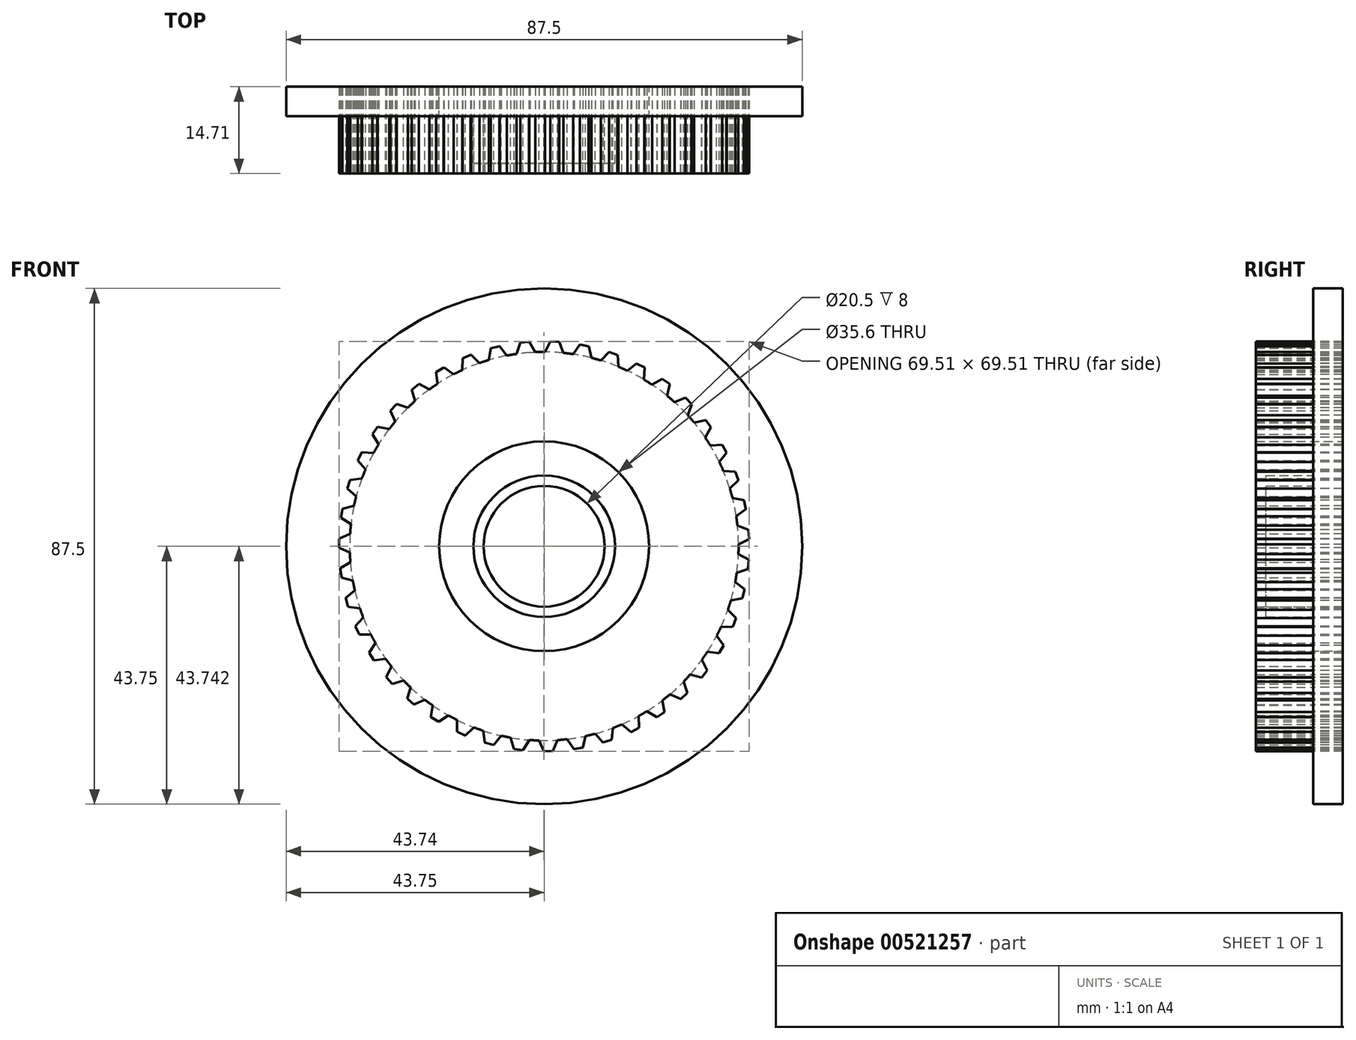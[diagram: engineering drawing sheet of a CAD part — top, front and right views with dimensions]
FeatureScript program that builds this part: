
annotation { "Feature Type Name" : "Feature", "Feature Type Description" : "" }
export const myFeature = defineFeature(function(context is Context, id is Id, definition is map)
    precondition{}
    {
        {
            var Q0;
            Q0=qCreatedBy(makeId("Front.planeOp"),FACE);
            var sketch = newSketch(context, id + "F0", { "sketchPlane" : qUnion([Q0])});
            skCircle(sketch, "E0", {"center": v(0, 0) * mm, "radius": 34.77 * mm, "construction": true});
            skCircle(sketch, "E1", {"center": v(0, 0) * mm, "radius": 10.25 * mm});
            skCircle(sketch, "E2", {"center": v(0, 0) * mm, "radius": 43.75 * mm});
            skCircle(sketch, "E3", {"center": v(0, 0) * mm, "radius": 12 * mm});
            skLineSegment(sketch, "E4", {"start": v(-2.5, 34.67) * mm, "end": v(2.5, 34.67) * mm, "construction": true});
            skCircle(sketch, "E5", {"center": v(0, 0) * mm, "radius": 32.97 * mm});
            skLineSegment(sketch, "E6", {"start": v(0, 0) * mm, "end": v(0, 46.74) * mm, "construction": true});
            skLineSegment(sketch, "E7", {"start": v(-2.5, 34.67) * mm, "end": v(-1.53, 32.93) * mm});
            skLineSegment(sketch, "E8", {"start": v(-1.53, 32.93) * mm, "end": v(0.13, 32.96) * mm});
            skLineSegment(sketch, "E9", {"start": v(0.13, 32.96) * mm, "end": v(1.03, 34.75) * mm});
            skLineSegment(sketch, "E10", {"start": v(1.03, 34.75) * mm, "end": v(2.5, 34.67) * mm});
            skLineSegment(sketch, "E11", {"start": v(-2.5, 34.67) * mm, "end": v(0, 0) * mm, "construction": true});
            skLineSegment(sketch, "E12", {"start": v(1.03, 34.75) * mm, "end": v(0, 0) * mm, "construction": true});
            skLineSegment(sketch, "E13", {"start": v(-2.5, 34.67) * mm, "end": v(-2.37, 32.88) * mm, "construction": true});
            skLineSegment(sketch, "E14", {"start": v(-2.37, 32.88) * mm, "end": v(0.13, 32.96) * mm});
            skLineSegment(sketch, "E15.1.0", {"start": v(-7.52, 33.94) * mm, "end": v(-6.3, 32.36) * mm});
            skLineSegment(sketch, "E15.1.1", {"start": v(-6.3, 32.36) * mm, "end": v(-4.67, 32.63) * mm});
            skLineSegment(sketch, "E15.1.2", {"start": v(-4.67, 32.63) * mm, "end": v(-4.05, 34.53) * mm});
            skLineSegment(sketch, "E15.1.3", {"start": v(-4.05, 34.53) * mm, "end": v(-2.58, 34.67) * mm});
            skLineSegment(sketch, "E15.2.0", {"start": v(-12.38, 32.48) * mm, "end": v(-10.95, 31.1) * mm});
            skLineSegment(sketch, "E15.2.1", {"start": v(-10.95, 31.1) * mm, "end": v(-9.37, 31.6) * mm});
            skLineSegment(sketch, "E15.2.2", {"start": v(-9.37, 31.6) * mm, "end": v(-9.03, 33.57) * mm});
            skLineSegment(sketch, "E15.2.3", {"start": v(-9.03, 33.57) * mm, "end": v(-7.6, 33.93) * mm});
            skLineSegment(sketch, "E15.3.0", {"start": v(-16.98, 30.34) * mm, "end": v(-15.36, 29.17) * mm});
            skLineSegment(sketch, "E15.3.1", {"start": v(-15.36, 29.17) * mm, "end": v(-13.88, 29.9) * mm});
            skLineSegment(sketch, "E15.3.2", {"start": v(-13.88, 29.9) * mm, "end": v(-13.82, 31.9) * mm});
            skLineSegment(sketch, "E15.3.3", {"start": v(-13.82, 31.9) * mm, "end": v(-12.45, 32.46) * mm});
            skLineSegment(sketch, "E15.4.0", {"start": v(-21.22, 27.54) * mm, "end": v(-19.44, 26.62) * mm});
            skLineSegment(sketch, "E15.4.1", {"start": v(-19.44, 26.62) * mm, "end": v(-18.08, 27.56) * mm});
            skLineSegment(sketch, "E15.4.2", {"start": v(-18.08, 27.56) * mm, "end": v(-18.32, 29.55) * mm});
            skLineSegment(sketch, "E15.4.3", {"start": v(-18.32, 29.55) * mm, "end": v(-17.05, 30.3) * mm});
            skLineSegment(sketch, "E15.5.0", {"start": v(-25, 24.16) * mm, "end": v(-23.11, 23.5) * mm});
            skLineSegment(sketch, "E15.5.1", {"start": v(-23.11, 23.5) * mm, "end": v(-21.9, 24.64) * mm});
            skLineSegment(sketch, "E15.5.2", {"start": v(-21.9, 24.64) * mm, "end": v(-22.43, 26.57) * mm});
            skLineSegment(sketch, "E15.5.3", {"start": v(-22.43, 26.57) * mm, "end": v(-21.28, 27.5) * mm});
            skLineSegment(sketch, "E15.6.0", {"start": v(-28.25, 20.26) * mm, "end": v(-26.29, 19.9) * mm});
            skLineSegment(sketch, "E15.6.1", {"start": v(-26.29, 19.9) * mm, "end": v(-25.26, 21.19) * mm});
            skLineSegment(sketch, "E15.6.2", {"start": v(-25.26, 21.19) * mm, "end": v(-26.05, 23.02) * mm});
            skLineSegment(sketch, "E15.6.3", {"start": v(-26.05, 23.02) * mm, "end": v(-25.05, 24.1) * mm});
            skLineSegment(sketch, "E15.7.0", {"start": v(-30.9, 15.93) * mm, "end": v(-28.9, 15.85) * mm});
            skLineSegment(sketch, "E15.7.1", {"start": v(-28.9, 15.85) * mm, "end": v(-28.07, 17.28) * mm});
            skLineSegment(sketch, "E15.7.2", {"start": v(-28.07, 17.28) * mm, "end": v(-29.13, 18.98) * mm});
            skLineSegment(sketch, "E15.7.3", {"start": v(-29.13, 18.98) * mm, "end": v(-28.3, 20.2) * mm});
            skLineSegment(sketch, "E15.8.0", {"start": v(-32.9, 11.26) * mm, "end": v(-30.9, 11.47) * mm});
            skLineSegment(sketch, "E15.8.1", {"start": v(-30.9, 11.47) * mm, "end": v(-30.29, 13.01) * mm});
            skLineSegment(sketch, "E15.8.2", {"start": v(-30.29, 13.01) * mm, "end": v(-31.58, 14.53) * mm});
            skLineSegment(sketch, "E15.8.3", {"start": v(-31.58, 14.53) * mm, "end": v(-30.94, 15.86) * mm});
            skLineSegment(sketch, "E15.9.0", {"start": v(-34.18, 6.35) * mm, "end": v(-32.25, 6.85) * mm});
            skLineSegment(sketch, "E15.9.1", {"start": v(-32.25, 6.85) * mm, "end": v(-31.86, 8.46) * mm});
            skLineSegment(sketch, "E15.9.2", {"start": v(-31.86, 8.46) * mm, "end": v(-33.36, 9.78) * mm});
            skLineSegment(sketch, "E15.9.3", {"start": v(-33.36, 9.78) * mm, "end": v(-32.92, 11.19) * mm});
            skLineSegment(sketch, "E15.10.0", {"start": v(-34.74, 1.3) * mm, "end": v(-32.9, 2.08) * mm});
            skLineSegment(sketch, "E15.10.1", {"start": v(-32.9, 2.08) * mm, "end": v(-32.75, 3.73) * mm});
            skLineSegment(sketch, "E15.10.2", {"start": v(-32.75, 3.73) * mm, "end": v(-34.43, 4.82) * mm});
            skLineSegment(sketch, "E15.10.3", {"start": v(-34.43, 4.82) * mm, "end": v(-34.2, 6.28) * mm});
            skLineSegment(sketch, "E15.11.0", {"start": v(-34.56, -3.76) * mm, "end": v(-32.85, -2.73) * mm});
            skLineSegment(sketch, "E15.11.1", {"start": v(-32.85, -2.73) * mm, "end": v(-32.95, -1.08) * mm});
            skLineSegment(sketch, "E15.11.2", {"start": v(-32.95, -1.08) * mm, "end": v(-34.76, -0.24) * mm});
            skLineSegment(sketch, "E15.11.3", {"start": v(-34.76, -0.24) * mm, "end": v(-34.74, 1.23) * mm});
            skLineSegment(sketch, "E15.12.0", {"start": v(-33.64, -8.76) * mm, "end": v(-32.1, -7.48) * mm});
            skLineSegment(sketch, "E15.12.1", {"start": v(-32.1, -7.48) * mm, "end": v(-32.44, -5.86) * mm});
            skLineSegment(sketch, "E15.12.2", {"start": v(-32.44, -5.86) * mm, "end": v(-34.36, -5.3) * mm});
            skLineSegment(sketch, "E15.12.3", {"start": v(-34.36, -5.3) * mm, "end": v(-34.55, -3.84) * mm});
            skLineSegment(sketch, "E15.13.0", {"start": v(-32.01, -13.56) * mm, "end": v(-30.67, -12.08) * mm});
            skLineSegment(sketch, "E15.13.1", {"start": v(-30.67, -12.08) * mm, "end": v(-31.24, -10.52) * mm});
            skLineSegment(sketch, "E15.13.2", {"start": v(-31.24, -10.52) * mm, "end": v(-33.22, -10.25) * mm});
            skLineSegment(sketch, "E15.13.3", {"start": v(-33.22, -10.25) * mm, "end": v(-33.62, -8.83) * mm});
            skLineSegment(sketch, "E15.14.0", {"start": v(-29.7, -18.08) * mm, "end": v(-28.59, -16.42) * mm});
            skLineSegment(sketch, "E15.14.1", {"start": v(-28.59, -16.42) * mm, "end": v(-29.38, -14.96) * mm});
            skLineSegment(sketch, "E15.14.2", {"start": v(-29.38, -14.96) * mm, "end": v(-31.37, -14.98) * mm});
            skLineSegment(sketch, "E15.14.3", {"start": v(-31.37, -14.98) * mm, "end": v(-31.98, -13.63) * mm});
            skLineSegment(sketch, "E15.15.0", {"start": v(-26.75, -22.2) * mm, "end": v(-25.9, -20.4) * mm});
            skLineSegment(sketch, "E15.15.1", {"start": v(-25.9, -20.4) * mm, "end": v(-26.88, -19.08) * mm});
            skLineSegment(sketch, "E15.15.2", {"start": v(-26.88, -19.08) * mm, "end": v(-28.86, -19.39) * mm});
            skLineSegment(sketch, "E15.15.3", {"start": v(-28.86, -19.39) * mm, "end": v(-29.66, -18.14) * mm});
            skLineSegment(sketch, "E15.16.0", {"start": v(-23.23, -25.87) * mm, "end": v(-22.65, -23.96) * mm});
            skLineSegment(sketch, "E15.16.1", {"start": v(-22.65, -23.96) * mm, "end": v(-23.82, -22.79) * mm});
            skLineSegment(sketch, "E15.16.2", {"start": v(-23.82, -22.79) * mm, "end": v(-25.73, -23.38) * mm});
            skLineSegment(sketch, "E15.16.3", {"start": v(-25.73, -23.38) * mm, "end": v(-26.7, -22.27) * mm});
            skLineSegment(sketch, "E15.17.0", {"start": v(-19.21, -28.97) * mm, "end": v(-18.92, -27) * mm});
            skLineSegment(sketch, "E15.17.1", {"start": v(-18.92, -27) * mm, "end": v(-20.25, -26.01) * mm});
            skLineSegment(sketch, "E15.17.2", {"start": v(-20.25, -26.01) * mm, "end": v(-22.05, -26.88) * mm});
            skLineSegment(sketch, "E15.17.3", {"start": v(-22.05, -26.88) * mm, "end": v(-23.17, -25.92) * mm});
            skLineSegment(sketch, "E15.18.0", {"start": v(-14.8, -31.46) * mm, "end": v(-14.78, -29.46) * mm});
            skLineSegment(sketch, "E15.18.1", {"start": v(-14.78, -29.46) * mm, "end": v(-16.25, -28.68) * mm});
            skLineSegment(sketch, "E15.18.2", {"start": v(-16.25, -28.68) * mm, "end": v(-17.9, -29.8) * mm});
            skLineSegment(sketch, "E15.18.3", {"start": v(-17.9, -29.8) * mm, "end": v(-19.15, -29.01) * mm});
            skLineSegment(sketch, "E15.19.0", {"start": v(-10.05, -33.28) * mm, "end": v(-10.34, -31.3) * mm});
            skLineSegment(sketch, "E15.19.1", {"start": v(-10.34, -31.3) * mm, "end": v(-11.9, -30.74) * mm});
            skLineSegment(sketch, "E15.19.2", {"start": v(-11.9, -30.74) * mm, "end": v(-13.37, -32.1) * mm});
            skLineSegment(sketch, "E15.19.3", {"start": v(-13.37, -32.1) * mm, "end": v(-14.72, -31.5) * mm});
            skLineSegment(sketch, "E15.20.0", {"start": v(-5.1, -34.39) * mm, "end": v(-5.67, -32.47) * mm});
            skLineSegment(sketch, "E15.20.1", {"start": v(-5.67, -32.47) * mm, "end": v(-7.3, -32.15) * mm});
            skLineSegment(sketch, "E15.20.2", {"start": v(-7.3, -32.15) * mm, "end": v(-8.56, -33.7) * mm});
            skLineSegment(sketch, "E15.20.3", {"start": v(-8.56, -33.7) * mm, "end": v(-9.98, -33.3) * mm});
            skLineSegment(sketch, "E15.21.0", {"start": v(-0.04, -34.76) * mm, "end": v(-0.88, -32.95) * mm});
            skLineSegment(sketch, "E15.21.1", {"start": v(-0.88, -32.95) * mm, "end": v(-2.53, -32.87) * mm});
            skLineSegment(sketch, "E15.21.2", {"start": v(-2.53, -32.87) * mm, "end": v(-3.56, -34.58) * mm});
            skLineSegment(sketch, "E15.21.3", {"start": v(-3.56, -34.58) * mm, "end": v(-5.02, -34.4) * mm});
            skLineSegment(sketch, "E15.22.0", {"start": v(5.02, -34.4) * mm, "end": v(3.93, -32.73) * mm});
            skLineSegment(sketch, "E15.22.1", {"start": v(3.93, -32.73) * mm, "end": v(2.28, -32.89) * mm});
            skLineSegment(sketch, "E15.22.2", {"start": v(2.28, -32.89) * mm, "end": v(1.51, -34.73) * mm});
            skLineSegment(sketch, "E15.22.3", {"start": v(1.51, -34.73) * mm, "end": v(0.04, -34.76) * mm});
            skLineSegment(sketch, "E15.23.0", {"start": v(9.98, -33.3) * mm, "end": v(8.65, -31.8) * mm});
            skLineSegment(sketch, "E15.23.1", {"start": v(8.65, -31.8) * mm, "end": v(7.04, -32.2) * mm});
            skLineSegment(sketch, "E15.23.2", {"start": v(7.04, -32.2) * mm, "end": v(6.55, -34.14) * mm});
            skLineSegment(sketch, "E15.23.3", {"start": v(6.55, -34.14) * mm, "end": v(5.1, -34.39) * mm});
            skLineSegment(sketch, "E15.24.0", {"start": v(14.72, -31.5) * mm, "end": v(13.2, -30.21) * mm});
            skLineSegment(sketch, "E15.24.1", {"start": v(13.2, -30.21) * mm, "end": v(11.66, -30.84) * mm});
            skLineSegment(sketch, "E15.24.2", {"start": v(11.66, -30.84) * mm, "end": v(11.46, -32.82) * mm});
            skLineSegment(sketch, "E15.24.3", {"start": v(11.46, -32.82) * mm, "end": v(10.05, -33.28) * mm});
            skLineSegment(sketch, "E15.25.0", {"start": v(19.15, -29.01) * mm, "end": v(17.45, -27.97) * mm});
            skLineSegment(sketch, "E15.25.1", {"start": v(17.45, -27.97) * mm, "end": v(16.02, -28.8) * mm});
            skLineSegment(sketch, "E15.25.2", {"start": v(16.02, -28.8) * mm, "end": v(16.11, -30.8) * mm});
            skLineSegment(sketch, "E15.25.3", {"start": v(16.11, -30.8) * mm, "end": v(14.8, -31.46) * mm});
            skLineSegment(sketch, "E15.26.0", {"start": v(23.17, -25.92) * mm, "end": v(21.33, -25.13) * mm});
            skLineSegment(sketch, "E15.26.1", {"start": v(21.33, -25.13) * mm, "end": v(20.05, -26.17) * mm});
            skLineSegment(sketch, "E15.26.2", {"start": v(20.05, -26.17) * mm, "end": v(20.43, -28.13) * mm});
            skLineSegment(sketch, "E15.26.3", {"start": v(20.43, -28.13) * mm, "end": v(19.21, -28.97) * mm});
            skLineSegment(sketch, "E15.27.0", {"start": v(26.7, -22.27) * mm, "end": v(24.77, -21.76) * mm});
            skLineSegment(sketch, "E15.27.1", {"start": v(24.77, -21.76) * mm, "end": v(23.64, -22.97) * mm});
            skLineSegment(sketch, "E15.27.2", {"start": v(23.64, -22.97) * mm, "end": v(24.3, -24.86) * mm});
            skLineSegment(sketch, "E15.27.3", {"start": v(24.3, -24.86) * mm, "end": v(23.23, -25.87) * mm});
            skLineSegment(sketch, "E15.28.0", {"start": v(29.66, -18.14) * mm, "end": v(27.67, -17.92) * mm});
            skLineSegment(sketch, "E15.28.1", {"start": v(27.67, -17.92) * mm, "end": v(26.74, -19.28) * mm});
            skLineSegment(sketch, "E15.28.2", {"start": v(26.74, -19.28) * mm, "end": v(27.67, -21.05) * mm});
            skLineSegment(sketch, "E15.28.3", {"start": v(27.67, -21.05) * mm, "end": v(26.75, -22.2) * mm});
            skLineSegment(sketch, "E15.29.0", {"start": v(31.98, -13.63) * mm, "end": v(29.98, -13.7) * mm});
            skLineSegment(sketch, "E15.29.1", {"start": v(29.98, -13.7) * mm, "end": v(29.26, -15.19) * mm});
            skLineSegment(sketch, "E15.29.2", {"start": v(29.26, -15.19) * mm, "end": v(30.44, -16.8) * mm});
            skLineSegment(sketch, "E15.29.3", {"start": v(30.44, -16.8) * mm, "end": v(29.7, -18.08) * mm});
            skLineSegment(sketch, "E15.30.0", {"start": v(33.62, -8.83) * mm, "end": v(31.66, -9.19) * mm});
            skLineSegment(sketch, "E15.30.1", {"start": v(31.66, -9.19) * mm, "end": v(31.16, -10.76) * mm});
            skLineSegment(sketch, "E15.30.2", {"start": v(31.16, -10.76) * mm, "end": v(32.56, -12.2) * mm});
            skLineSegment(sketch, "E15.30.3", {"start": v(32.56, -12.2) * mm, "end": v(32.01, -13.56) * mm});
            skLineSegment(sketch, "E15.31.0", {"start": v(34.55, -3.84) * mm, "end": v(32.66, -4.48) * mm});
            skLineSegment(sketch, "E15.31.1", {"start": v(32.66, -4.48) * mm, "end": v(32.4, -6.11) * mm});
            skLineSegment(sketch, "E15.31.2", {"start": v(32.4, -6.11) * mm, "end": v(33.99, -7.32) * mm});
            skLineSegment(sketch, "E15.31.3", {"start": v(33.99, -7.32) * mm, "end": v(33.64, -8.76) * mm});
            skLineSegment(sketch, "E15.32.0", {"start": v(34.74, 1.23) * mm, "end": v(32.96, 0.32) * mm});
            skLineSegment(sketch, "E15.32.1", {"start": v(32.96, 0.32) * mm, "end": v(32.94, -1.33) * mm});
            skLineSegment(sketch, "E15.32.2", {"start": v(32.94, -1.33) * mm, "end": v(34.69, -2.3) * mm});
            skLineSegment(sketch, "E15.32.3", {"start": v(34.69, -2.3) * mm, "end": v(34.56, -3.76) * mm});
            skLineSegment(sketch, "E15.33.0", {"start": v(34.2, 6.28) * mm, "end": v(32.56, 5.12) * mm});
            skLineSegment(sketch, "E15.33.1", {"start": v(32.56, 5.12) * mm, "end": v(32.78, 3.48) * mm});
            skLineSegment(sketch, "E15.33.2", {"start": v(32.78, 3.48) * mm, "end": v(34.65, 2.78) * mm});
            skLineSegment(sketch, "E15.33.3", {"start": v(34.65, 2.78) * mm, "end": v(34.74, 1.3) * mm});
            skLineSegment(sketch, "E15.34.0", {"start": v(32.92, 11.19) * mm, "end": v(31.47, 9.8) * mm});
            skLineSegment(sketch, "E15.34.1", {"start": v(31.47, 9.8) * mm, "end": v(31.93, 8.21) * mm});
            skLineSegment(sketch, "E15.34.2", {"start": v(31.93, 8.21) * mm, "end": v(33.88, 7.8) * mm});
            skLineSegment(sketch, "E15.34.3", {"start": v(33.88, 7.8) * mm, "end": v(34.18, 6.35) * mm});
            skLineSegment(sketch, "E15.35.0", {"start": v(30.94, 15.86) * mm, "end": v(29.7, 14.28) * mm});
            skLineSegment(sketch, "E15.35.1", {"start": v(29.7, 14.28) * mm, "end": v(30.39, 12.77) * mm});
            skLineSegment(sketch, "E15.35.2", {"start": v(30.39, 12.77) * mm, "end": v(32.38, 12.65) * mm});
            skLineSegment(sketch, "E15.35.3", {"start": v(32.38, 12.65) * mm, "end": v(32.9, 11.26) * mm});
            skLineSegment(sketch, "E15.36.0", {"start": v(28.3, 20.2) * mm, "end": v(27.31, 18.46) * mm});
            skLineSegment(sketch, "E15.36.1", {"start": v(27.31, 18.46) * mm, "end": v(28.2, 17.06) * mm});
            skLineSegment(sketch, "E15.36.2", {"start": v(28.2, 17.06) * mm, "end": v(30.2, 17.23) * mm});
            skLineSegment(sketch, "E15.36.3", {"start": v(30.2, 17.23) * mm, "end": v(30.9, 15.93) * mm});
            skLineSegment(sketch, "E15.37.0", {"start": v(25.05, 24.1) * mm, "end": v(24.33, 22.24) * mm});
            skLineSegment(sketch, "E15.37.1", {"start": v(24.33, 22.24) * mm, "end": v(25.42, 20.99) * mm});
            skLineSegment(sketch, "E15.37.2", {"start": v(25.42, 20.99) * mm, "end": v(27.37, 21.44) * mm});
            skLineSegment(sketch, "E15.37.3", {"start": v(27.37, 21.44) * mm, "end": v(28.25, 20.26) * mm});
            skLineSegment(sketch, "E15.38.0", {"start": v(21.28, 27.5) * mm, "end": v(20.84, 25.54) * mm});
            skLineSegment(sketch, "E15.38.1", {"start": v(20.84, 25.54) * mm, "end": v(22.1, 24.47) * mm});
            skLineSegment(sketch, "E15.38.2", {"start": v(22.1, 24.47) * mm, "end": v(23.95, 25.2) * mm});
            skLineSegment(sketch, "E15.38.3", {"start": v(23.95, 25.2) * mm, "end": v(25, 24.16) * mm});
            skLineSegment(sketch, "E15.39.0", {"start": v(17.05, 30.3) * mm, "end": v(16.9, 28.3) * mm});
            skLineSegment(sketch, "E15.39.1", {"start": v(16.9, 28.3) * mm, "end": v(18.3, 27.42) * mm});
            skLineSegment(sketch, "E15.39.2", {"start": v(18.3, 27.42) * mm, "end": v(20.03, 28.42) * mm});
            skLineSegment(sketch, "E15.39.3", {"start": v(20.03, 28.42) * mm, "end": v(21.22, 27.54) * mm});
            skLineSegment(sketch, "E15.40.0", {"start": v(12.45, 32.46) * mm, "end": v(12.6, 30.46) * mm});
            skLineSegment(sketch, "E15.40.1", {"start": v(12.6, 30.46) * mm, "end": v(14.1, 29.8) * mm});
            skLineSegment(sketch, "E15.40.2", {"start": v(14.1, 29.8) * mm, "end": v(15.68, 31.03) * mm});
            skLineSegment(sketch, "E15.40.3", {"start": v(15.68, 31.03) * mm, "end": v(16.98, 30.34) * mm});
            skLineSegment(sketch, "E15.41.0", {"start": v(7.6, 33.93) * mm, "end": v(8.02, 31.97) * mm});
            skLineSegment(sketch, "E15.41.1", {"start": v(8.02, 31.97) * mm, "end": v(9.62, 31.53) * mm});
            skLineSegment(sketch, "E15.41.2", {"start": v(9.62, 31.53) * mm, "end": v(11, 32.98) * mm});
            skLineSegment(sketch, "E15.41.3", {"start": v(11, 32.98) * mm, "end": v(12.38, 32.48) * mm});
            skLineSegment(sketch, "E15.42.0", {"start": v(2.58, 34.67) * mm, "end": v(3.28, 32.8) * mm});
            skLineSegment(sketch, "E15.42.1", {"start": v(3.28, 32.8) * mm, "end": v(4.93, 32.6) * mm});
            skLineSegment(sketch, "E15.42.2", {"start": v(4.93, 32.6) * mm, "end": v(6.07, 34.23) * mm});
            skLineSegment(sketch, "E15.42.3", {"start": v(6.07, 34.23) * mm, "end": v(7.52, 33.94) * mm});
            skLineSegment(sketch, "E16", {"start": v(2.5, 34.67) * mm, "end": v(2.58, 34.67) * mm});
            skLineSegment(sketch, "E17.1.0", {"start": v(-2.58, 34.67) * mm, "end": v(-2.5, 34.67) * mm});
            skLineSegment(sketch, "E17.2.0", {"start": v(-7.6, 33.93) * mm, "end": v(-7.52, 33.94) * mm});
            skLineSegment(sketch, "E17.3.0", {"start": v(-12.45, 32.46) * mm, "end": v(-12.38, 32.48) * mm});
            skLineSegment(sketch, "E17.4.0", {"start": v(-17.05, 30.3) * mm, "end": v(-16.98, 30.34) * mm});
            skLineSegment(sketch, "E17.5.0", {"start": v(-21.28, 27.5) * mm, "end": v(-21.22, 27.54) * mm});
            skLineSegment(sketch, "E17.6.0", {"start": v(-25.05, 24.1) * mm, "end": v(-25, 24.16) * mm});
            skLineSegment(sketch, "E17.7.0", {"start": v(-28.3, 20.2) * mm, "end": v(-28.25, 20.26) * mm});
            skLineSegment(sketch, "E17.8.0", {"start": v(-30.94, 15.86) * mm, "end": v(-30.9, 15.93) * mm});
            skLineSegment(sketch, "E17.9.0", {"start": v(-32.92, 11.19) * mm, "end": v(-32.9, 11.26) * mm});
            skLineSegment(sketch, "E17.10.0", {"start": v(-34.2, 6.28) * mm, "end": v(-34.18, 6.35) * mm});
            skLineSegment(sketch, "E17.11.0", {"start": v(-34.74, 1.23) * mm, "end": v(-34.74, 1.3) * mm});
            skLineSegment(sketch, "E17.12.0", {"start": v(-34.55, -3.84) * mm, "end": v(-34.56, -3.76) * mm});
            skLineSegment(sketch, "E17.13.0", {"start": v(-33.62, -8.83) * mm, "end": v(-33.64, -8.76) * mm});
            skLineSegment(sketch, "E17.14.0", {"start": v(-31.98, -13.63) * mm, "end": v(-32.01, -13.56) * mm});
            skLineSegment(sketch, "E17.15.0", {"start": v(-29.66, -18.14) * mm, "end": v(-29.7, -18.08) * mm});
            skLineSegment(sketch, "E17.16.0", {"start": v(-26.7, -22.27) * mm, "end": v(-26.75, -22.2) * mm});
            skLineSegment(sketch, "E17.17.0", {"start": v(-23.17, -25.92) * mm, "end": v(-23.23, -25.87) * mm});
            skLineSegment(sketch, "E17.18.0", {"start": v(-19.15, -29.01) * mm, "end": v(-19.21, -28.97) * mm});
            skLineSegment(sketch, "E17.19.0", {"start": v(-14.72, -31.5) * mm, "end": v(-14.8, -31.46) * mm});
            skLineSegment(sketch, "E17.20.0", {"start": v(-9.98, -33.3) * mm, "end": v(-10.05, -33.28) * mm});
            skLineSegment(sketch, "E17.21.0", {"start": v(-5.02, -34.4) * mm, "end": v(-5.1, -34.39) * mm});
            skLineSegment(sketch, "E17.22.0", {"start": v(0.04, -34.76) * mm, "end": v(-0.04, -34.76) * mm});
            skLineSegment(sketch, "E17.23.0", {"start": v(5.1, -34.39) * mm, "end": v(5.02, -34.4) * mm});
            skLineSegment(sketch, "E17.24.0", {"start": v(10.05, -33.28) * mm, "end": v(9.98, -33.3) * mm});
            skLineSegment(sketch, "E17.25.0", {"start": v(14.8, -31.46) * mm, "end": v(14.72, -31.5) * mm});
            skLineSegment(sketch, "E17.26.0", {"start": v(19.21, -28.97) * mm, "end": v(19.15, -29.01) * mm});
            skLineSegment(sketch, "E17.27.0", {"start": v(23.23, -25.87) * mm, "end": v(23.17, -25.92) * mm});
            skLineSegment(sketch, "E17.28.0", {"start": v(26.75, -22.2) * mm, "end": v(26.7, -22.27) * mm});
            skLineSegment(sketch, "E17.29.0", {"start": v(29.7, -18.08) * mm, "end": v(29.66, -18.14) * mm});
            skLineSegment(sketch, "E17.30.0", {"start": v(32.01, -13.56) * mm, "end": v(31.98, -13.63) * mm});
            skLineSegment(sketch, "E17.31.0", {"start": v(33.64, -8.76) * mm, "end": v(33.62, -8.83) * mm});
            skLineSegment(sketch, "E17.32.0", {"start": v(34.56, -3.76) * mm, "end": v(34.55, -3.84) * mm});
            skLineSegment(sketch, "E17.33.0", {"start": v(34.74, 1.3) * mm, "end": v(34.74, 1.23) * mm});
            skLineSegment(sketch, "E17.34.0", {"start": v(34.18, 6.35) * mm, "end": v(34.2, 6.28) * mm});
            skLineSegment(sketch, "E17.35.0", {"start": v(32.9, 11.26) * mm, "end": v(32.92, 11.19) * mm});
            skLineSegment(sketch, "E17.36.0", {"start": v(30.9, 15.93) * mm, "end": v(30.94, 15.86) * mm});
            skLineSegment(sketch, "E17.37.0", {"start": v(28.25, 20.26) * mm, "end": v(28.3, 20.2) * mm});
            skLineSegment(sketch, "E17.38.0", {"start": v(25, 24.16) * mm, "end": v(25.05, 24.1) * mm});
            skLineSegment(sketch, "E17.39.0", {"start": v(21.22, 27.54) * mm, "end": v(21.28, 27.5) * mm});
            skLineSegment(sketch, "E17.40.0", {"start": v(16.98, 30.34) * mm, "end": v(17.05, 30.3) * mm});
            skLineSegment(sketch, "E17.41.0", {"start": v(12.38, 32.48) * mm, "end": v(12.45, 32.46) * mm});
            skLineSegment(sketch, "E17.42.0", {"start": v(7.52, 33.94) * mm, "end": v(7.6, 33.93) * mm});
            skSolve(sketch);
        }
        {
            var Q0;
            {var subQ1=sQuery(id+"F0.wireOp",EDGE,"E15.4.0");Q0=makeQuery(id+"F0.imprint","IMPRINT",FACE,{"disambiguationData":[TD([[makeQuery(id+"F0.imprint","IMPRINT",EDGE,{"derivedFrom":subQ1}),-1.0]])]});}
            var Q1;
            {var subQ1=sQuery(id+"F0.wireOp",EDGE,"E15.28.0");Q1=makeQuery(id+"F0.imprint","IMPRINT",FACE,{"disambiguationData":[TD([[makeQuery(id+"F0.imprint","IMPRINT",EDGE,{"derivedFrom":subQ1}),-1.0]])]});}
            var Q2;
            {var subQ1=sQuery(id+"F0.wireOp",EDGE,"E15.41.0");Q2=makeQuery(id+"F0.imprint","IMPRINT",FACE,{"disambiguationData":[TD([[makeQuery(id+"F0.imprint","IMPRINT",EDGE,{"derivedFrom":subQ1}),-1.0]])]});}
            var Q3;
            {var subQ1=sQuery(id+"F0.wireOp",EDGE,"E15.2.0");Q3=makeQuery(id+"F0.imprint","IMPRINT",FACE,{"disambiguationData":[TD([[makeQuery(id+"F0.imprint","IMPRINT",EDGE,{"derivedFrom":subQ1}),-1.0]])]});}
            var Q4;
            {var subQ1=sQuery(id+"F0.wireOp",EDGE,"E15.10.0");Q4=makeQuery(id+"F0.imprint","IMPRINT",FACE,{"disambiguationData":[TD([[makeQuery(id+"F0.imprint","IMPRINT",EDGE,{"derivedFrom":subQ1}),-1.0]])]});}
            var Q5;
            {var subQ1=sQuery(id+"F0.wireOp",EDGE,"E15.26.0");Q5=makeQuery(id+"F0.imprint","IMPRINT",FACE,{"disambiguationData":[TD([[makeQuery(id+"F0.imprint","IMPRINT",EDGE,{"derivedFrom":subQ1}),-1.0]])]});}
            var Q6;
            {var subQ1=sQuery(id+"F0.wireOp",EDGE,"E15.18.0");Q6=makeQuery(id+"F0.imprint","IMPRINT",FACE,{"disambiguationData":[TD([[makeQuery(id+"F0.imprint","IMPRINT",EDGE,{"derivedFrom":subQ1}),-1.0]])]});}
            var Q7;
            {var subQ1=sQuery(id+"F0.wireOp",EDGE,"E15.6.0");Q7=makeQuery(id+"F0.imprint","IMPRINT",FACE,{"disambiguationData":[TD([[makeQuery(id+"F0.imprint","IMPRINT",EDGE,{"derivedFrom":subQ1}),-1.0]])]});}
            var Q8;
            {var subQ1=sQuery(id+"F0.wireOp",EDGE,"E15.14.0");Q8=makeQuery(id+"F0.imprint","IMPRINT",FACE,{"disambiguationData":[TD([[makeQuery(id+"F0.imprint","IMPRINT",EDGE,{"derivedFrom":subQ1}),-1.0]])]});}
            var Q9;
            {var subQ1=sQuery(id+"F0.wireOp",EDGE,"E15.22.0");Q9=makeQuery(id+"F0.imprint","IMPRINT",FACE,{"disambiguationData":[TD([[makeQuery(id+"F0.imprint","IMPRINT",EDGE,{"derivedFrom":subQ1}),-1.0]])]});}
            var Q10;
            {var subQ1=sQuery(id+"F0.wireOp",EDGE,"E15.30.0");Q10=makeQuery(id+"F0.imprint","IMPRINT",FACE,{"disambiguationData":[TD([[makeQuery(id+"F0.imprint","IMPRINT",EDGE,{"derivedFrom":subQ1}),-1.0]])]});}
            var Q11;
            {var subQ1=sQuery(id+"F0.wireOp",EDGE,"E15.31.0");Q11=makeQuery(id+"F0.imprint","IMPRINT",FACE,{"disambiguationData":[TD([[makeQuery(id+"F0.imprint","IMPRINT",EDGE,{"derivedFrom":subQ1}),-1.0]])]});}
            var Q12;
            {var subQ1=sQuery(id+"F0.wireOp",EDGE,"E15.15.0");Q12=makeQuery(id+"F0.imprint","IMPRINT",FACE,{"disambiguationData":[TD([[makeQuery(id+"F0.imprint","IMPRINT",EDGE,{"derivedFrom":subQ1}),-1.0]])]});}
            var Q13;
            {var subQ1=sQuery(id+"F0.wireOp",EDGE,"E15.7.0");Q13=makeQuery(id+"F0.imprint","IMPRINT",FACE,{"disambiguationData":[TD([[makeQuery(id+"F0.imprint","IMPRINT",EDGE,{"derivedFrom":subQ1}),-1.0]])]});}
            var Q14;
            {var subQ1=sQuery(id+"F0.wireOp",EDGE,"E15.25.0");Q14=makeQuery(id+"F0.imprint","IMPRINT",FACE,{"disambiguationData":[TD([[makeQuery(id+"F0.imprint","IMPRINT",EDGE,{"derivedFrom":subQ1}),-1.0]])]});}
            var Q15;
            {var subQ1=sQuery(id+"F0.wireOp",EDGE,"E15.39.0");Q15=makeQuery(id+"F0.imprint","IMPRINT",FACE,{"disambiguationData":[TD([[makeQuery(id+"F0.imprint","IMPRINT",EDGE,{"derivedFrom":subQ1}),-1.0]])]});}
            var Q16;
            {var subQ1=sQuery(id+"F0.wireOp",EDGE,"E15.34.0");Q16=makeQuery(id+"F0.imprint","IMPRINT",FACE,{"disambiguationData":[TD([[makeQuery(id+"F0.imprint","IMPRINT",EDGE,{"derivedFrom":subQ1}),-1.0]])]});}
            var Q17;
            {var subQ1=sQuery(id+"F0.wireOp",EDGE,"E15.35.0");Q17=makeQuery(id+"F0.imprint","IMPRINT",FACE,{"disambiguationData":[TD([[makeQuery(id+"F0.imprint","IMPRINT",EDGE,{"derivedFrom":subQ1}),-1.0]])]});}
            var Q18;
            {var subQ0=sQuery(id+"F0.wireOp",EDGE,"E15.36.0");Q18=makeQuery(id+"F0.imprint","IMPRINT",FACE,{"disambiguationData":[TD([[makeQuery(id+"F0.imprint","IMPRINT",EDGE,{"derivedFrom":subQ0}),-1.0]])]});}
            var Q19;
            {var subQ1=sQuery(id+"F0.wireOp",EDGE,"E15.37.0");Q19=makeQuery(id+"F0.imprint","IMPRINT",FACE,{"disambiguationData":[TD([[makeQuery(id+"F0.imprint","IMPRINT",EDGE,{"derivedFrom":subQ1}),-1.0]])]});}
            var Q20;
            {var subQ1=sQuery(id+"F0.wireOp",EDGE,"E15.1.0");Q20=makeQuery(id+"F0.imprint","IMPRINT",FACE,{"disambiguationData":[TD([[makeQuery(id+"F0.imprint","IMPRINT",EDGE,{"derivedFrom":subQ1}),-1.0]])]});}
            var Q21;
            {var subQ1=sQuery(id+"F0.wireOp",EDGE,"E15.17.0");Q21=makeQuery(id+"F0.imprint","IMPRINT",FACE,{"disambiguationData":[TD([[makeQuery(id+"F0.imprint","IMPRINT",EDGE,{"derivedFrom":subQ1}),-1.0]])]});}
            var Q22;
            {var subQ1=sQuery(id+"F0.wireOp",EDGE,"E15.9.0");Q22=makeQuery(id+"F0.imprint","IMPRINT",FACE,{"disambiguationData":[TD([[makeQuery(id+"F0.imprint","IMPRINT",EDGE,{"derivedFrom":subQ1}),-1.0]])]});}
            var Q23;
            {var subQ1=sQuery(id+"F0.wireOp",EDGE,"E15.40.0");Q23=makeQuery(id+"F0.imprint","IMPRINT",FACE,{"disambiguationData":[TD([[makeQuery(id+"F0.imprint","IMPRINT",EDGE,{"derivedFrom":subQ1}),-1.0]])]});}
            var Q24;
            {var subQ1=sQuery(id+"F0.wireOp",EDGE,"E15.38.0");Q24=makeQuery(id+"F0.imprint","IMPRINT",FACE,{"disambiguationData":[TD([[makeQuery(id+"F0.imprint","IMPRINT",EDGE,{"derivedFrom":subQ1}),-1.0]])]});}
            var Q25;
            {var subQ1=sQuery(id+"F0.wireOp",EDGE,"E15.32.0");Q25=makeQuery(id+"F0.imprint","IMPRINT",FACE,{"disambiguationData":[TD([[makeQuery(id+"F0.imprint","IMPRINT",EDGE,{"derivedFrom":subQ1}),-1.0]])]});}
            var Q26;
            {var subQ1=sQuery(id+"F0.wireOp",EDGE,"E15.33.0");Q26=makeQuery(id+"F0.imprint","IMPRINT",FACE,{"disambiguationData":[TD([[makeQuery(id+"F0.imprint","IMPRINT",EDGE,{"derivedFrom":subQ1}),-1.0]])]});}
            var Q27;
            {var subQ1=sQuery(id+"F0.wireOp",EDGE,"E15.21.0");Q27=makeQuery(id+"F0.imprint","IMPRINT",FACE,{"disambiguationData":[TD([[makeQuery(id+"F0.imprint","IMPRINT",EDGE,{"derivedFrom":subQ1}),-1.0]])]});}
            var Q28;
            {var subQ1=sQuery(id+"F0.wireOp",EDGE,"E15.5.0");Q28=makeQuery(id+"F0.imprint","IMPRINT",FACE,{"disambiguationData":[TD([[makeQuery(id+"F0.imprint","IMPRINT",EDGE,{"derivedFrom":subQ1}),-1.0]])]});}
            var Q29;
            {var subQ1=sQuery(id+"F0.wireOp",EDGE,"E15.29.0");Q29=makeQuery(id+"F0.imprint","IMPRINT",FACE,{"disambiguationData":[TD([[makeQuery(id+"F0.imprint","IMPRINT",EDGE,{"derivedFrom":subQ1}),-1.0]])]});}
            var Q30;
            {var subQ1=sQuery(id+"F0.wireOp",EDGE,"E15.13.0");Q30=makeQuery(id+"F0.imprint","IMPRINT",FACE,{"disambiguationData":[TD([[makeQuery(id+"F0.imprint","IMPRINT",EDGE,{"derivedFrom":subQ1}),-1.0]])]});}
            var Q31;
            {var subQ1=sQuery(id+"F0.wireOp",EDGE,"E15.16.0");Q31=makeQuery(id+"F0.imprint","IMPRINT",FACE,{"disambiguationData":[TD([[makeQuery(id+"F0.imprint","IMPRINT",EDGE,{"derivedFrom":subQ1}),-1.0]])]});}
            var Q32;
            {var subQ1=sQuery(id+"F0.wireOp",EDGE,"E15.8.0");Q32=makeQuery(id+"F0.imprint","IMPRINT",FACE,{"disambiguationData":[TD([[makeQuery(id+"F0.imprint","IMPRINT",EDGE,{"derivedFrom":subQ1}),-1.0]])]});}
            var Q33;
            {var subQ1=sQuery(id+"F0.wireOp",EDGE,"E15.24.0");Q33=makeQuery(id+"F0.imprint","IMPRINT",FACE,{"disambiguationData":[TD([[makeQuery(id+"F0.imprint","IMPRINT",EDGE,{"derivedFrom":subQ1}),-1.0]])]});}
            var Q34;
            {var subQ1=sQuery(id+"F0.wireOp",EDGE,"E15.3.0");Q34=makeQuery(id+"F0.imprint","IMPRINT",FACE,{"disambiguationData":[TD([[makeQuery(id+"F0.imprint","IMPRINT",EDGE,{"derivedFrom":subQ1}),-1.0]])]});}
            var Q35;
            {var subQ1=sQuery(id+"F0.wireOp",EDGE,"E15.11.0");Q35=makeQuery(id+"F0.imprint","IMPRINT",FACE,{"disambiguationData":[TD([[makeQuery(id+"F0.imprint","IMPRINT",EDGE,{"derivedFrom":subQ1}),-1.0]])]});}
            var Q36;
            {var subQ1=sQuery(id+"F0.wireOp",EDGE,"E15.19.0");Q36=makeQuery(id+"F0.imprint","IMPRINT",FACE,{"disambiguationData":[TD([[makeQuery(id+"F0.imprint","IMPRINT",EDGE,{"derivedFrom":subQ1}),-1.0]])]});}
            var Q37;
            {var subQ1=sQuery(id+"F0.wireOp",EDGE,"E15.27.0");Q37=makeQuery(id+"F0.imprint","IMPRINT",FACE,{"disambiguationData":[TD([[makeQuery(id+"F0.imprint","IMPRINT",EDGE,{"derivedFrom":subQ1}),-1.0]])]});}
            var Q38;
            {var subQ1=sQuery(id+"F0.wireOp",EDGE,"E15.20.0");Q38=makeQuery(id+"F0.imprint","IMPRINT",FACE,{"disambiguationData":[TD([[makeQuery(id+"F0.imprint","IMPRINT",EDGE,{"derivedFrom":subQ1}),-1.0]])]});}
            var Q39;
            {var subQ1=sQuery(id+"F0.wireOp",EDGE,"E15.12.0");Q39=makeQuery(id+"F0.imprint","IMPRINT",FACE,{"disambiguationData":[TD([[makeQuery(id+"F0.imprint","IMPRINT",EDGE,{"derivedFrom":subQ1}),-1.0]])]});}
            var Q40;
            {var subQ0=sQuery(id+"F0.wireOp",EDGE,"E15.32.1");Q40=makeQuery(id+"F0.imprint","IMPRINT",FACE,{"disambiguationData":[TD([[makeQuery(id+"F0.imprint","IMPRINT",EDGE,{"derivedFrom":subQ0}),1.0]])]});}
            var Q41;
            {var subQ0=sQuery(id+"F0.wireOp",EDGE,"E15.7.1");Q41=makeQuery(id+"F0.imprint","IMPRINT",FACE,{"disambiguationData":[TD([[makeQuery(id+"F0.imprint","IMPRINT",EDGE,{"derivedFrom":subQ0}),1.0]])]});}
            var Q42;
            {var subQ0=sQuery(id+"F0.wireOp",EDGE,"E15.23.1");Q42=makeQuery(id+"F0.imprint","IMPRINT",FACE,{"disambiguationData":[TD([[makeQuery(id+"F0.imprint","IMPRINT",EDGE,{"derivedFrom":subQ0}),1.0]])]});}
            var Q43;
            {var subQ0=sQuery(id+"F0.wireOp",EDGE,"E15.28.1");Q43=makeQuery(id+"F0.imprint","IMPRINT",FACE,{"disambiguationData":[TD([[makeQuery(id+"F0.imprint","IMPRINT",EDGE,{"derivedFrom":subQ0}),1.0]])]});}
            var Q44;
            {var subQ0=sQuery(id+"F0.wireOp",EDGE,"E15.8.1");Q44=makeQuery(id+"F0.imprint","IMPRINT",FACE,{"disambiguationData":[TD([[makeQuery(id+"F0.imprint","IMPRINT",EDGE,{"derivedFrom":subQ0}),1.0]])]});}
            var Q45;
            {var subQ1=sQuery(id+"F0.wireOp",EDGE,"E9");Q45=makeQuery(id+"F0.imprint","IMPRINT",FACE,{"disambiguationData":[TD([[makeQuery(id+"F0.imprint","IMPRINT",EDGE,{"derivedFrom":subQ1}),-1.0]])]});}
            var Q46;
            {var subQ1=sQuery(id+"F0.wireOp",EDGE,"E15.23.0");Q46=makeQuery(id+"F0.imprint","IMPRINT",FACE,{"disambiguationData":[TD([[makeQuery(id+"F0.imprint","IMPRINT",EDGE,{"derivedFrom":subQ1}),-1.0]])]});}
            var Q47;
            {var subQ0=sQuery(id+"F0.wireOp",EDGE,"E15.13.1");Q47=makeQuery(id+"F0.imprint","IMPRINT",FACE,{"disambiguationData":[TD([[makeQuery(id+"F0.imprint","IMPRINT",EDGE,{"derivedFrom":subQ0}),1.0]])]});}
            var Q48;
            {var subQ0=sQuery(id+"F0.wireOp",EDGE,"E15.5.1");Q48=makeQuery(id+"F0.imprint","IMPRINT",FACE,{"disambiguationData":[TD([[makeQuery(id+"F0.imprint","IMPRINT",EDGE,{"derivedFrom":subQ0}),1.0]])]});}
            var Q49;
            {var subQ0=sQuery(id+"F0.wireOp",EDGE,"E15.30.1");Q49=makeQuery(id+"F0.imprint","IMPRINT",FACE,{"disambiguationData":[TD([[makeQuery(id+"F0.imprint","IMPRINT",EDGE,{"derivedFrom":subQ0}),1.0]])]});}
            var Q50;
            {var subQ0=sQuery(id+"F0.wireOp",EDGE,"E15.22.1");Q50=makeQuery(id+"F0.imprint","IMPRINT",FACE,{"disambiguationData":[TD([[makeQuery(id+"F0.imprint","IMPRINT",EDGE,{"derivedFrom":subQ0}),1.0]])]});}
            var Q51;
            {var subQ0=sQuery(id+"F0.wireOp",EDGE,"E15.14.1");Q51=makeQuery(id+"F0.imprint","IMPRINT",FACE,{"disambiguationData":[TD([[makeQuery(id+"F0.imprint","IMPRINT",EDGE,{"derivedFrom":subQ0}),1.0]])]});}
            var Q52;
            {var subQ0=sQuery(id+"F0.wireOp",EDGE,"E15.40.1");Q52=makeQuery(id+"F0.imprint","IMPRINT",FACE,{"disambiguationData":[TD([[makeQuery(id+"F0.imprint","IMPRINT",EDGE,{"derivedFrom":subQ0}),1.0]])]});}
            var Q53;
            {var subQ1=sQuery(id+"F0.wireOp",EDGE,"E7");Q53=makeQuery(id+"F0.imprint","IMPRINT",FACE,{"disambiguationData":[TD([[makeQuery(id+"F0.imprint","IMPRINT",EDGE,{"derivedFrom":subQ1}),-1.0]])]});}
            var Q54;
            {var subQ0=sQuery(id+"F0.wireOp",EDGE,"E15.11.1");Q54=makeQuery(id+"F0.imprint","IMPRINT",FACE,{"disambiguationData":[TD([[makeQuery(id+"F0.imprint","IMPRINT",EDGE,{"derivedFrom":subQ0}),1.0]])]});}
            var Q55;
            {var subQ0=sQuery(id+"F0.wireOp",EDGE,"E15.10.1");Q55=makeQuery(id+"F0.imprint","IMPRINT",FACE,{"disambiguationData":[TD([[makeQuery(id+"F0.imprint","IMPRINT",EDGE,{"derivedFrom":subQ0}),1.0]])]});}
            var Q56;
            {var subQ0=sQuery(id+"F0.wireOp",EDGE,"E15.2.1");Q56=makeQuery(id+"F0.imprint","IMPRINT",FACE,{"disambiguationData":[TD([[makeQuery(id+"F0.imprint","IMPRINT",EDGE,{"derivedFrom":subQ0}),1.0]])]});}
            var Q57;
            {var subQ0=sQuery(id+"F0.wireOp",EDGE,"E15.12.1");Q57=makeQuery(id+"F0.imprint","IMPRINT",FACE,{"disambiguationData":[TD([[makeQuery(id+"F0.imprint","IMPRINT",EDGE,{"derivedFrom":subQ0}),1.0]])]});}
            var Q58;
            {var subQ0=sQuery(id+"F0.wireOp",EDGE,"E15.24.1");Q58=makeQuery(id+"F0.imprint","IMPRINT",FACE,{"disambiguationData":[TD([[makeQuery(id+"F0.imprint","IMPRINT",EDGE,{"derivedFrom":subQ0}),1.0]])]});}
            var Q59;
            {var subQ0=sQuery(id+"F0.wireOp",EDGE,"E15.15.1");Q59=makeQuery(id+"F0.imprint","IMPRINT",FACE,{"disambiguationData":[TD([[makeQuery(id+"F0.imprint","IMPRINT",EDGE,{"derivedFrom":subQ0}),1.0]])]});}
            var Q60;
            {var subQ0=sQuery(id+"F0.wireOp",EDGE,"E15.31.1");Q60=makeQuery(id+"F0.imprint","IMPRINT",FACE,{"disambiguationData":[TD([[makeQuery(id+"F0.imprint","IMPRINT",EDGE,{"derivedFrom":subQ0}),1.0]])]});}
            var Q61;
            {var subQ0=sQuery(id+"F0.wireOp",EDGE,"E15.20.1");Q61=makeQuery(id+"F0.imprint","IMPRINT",FACE,{"disambiguationData":[TD([[makeQuery(id+"F0.imprint","IMPRINT",EDGE,{"derivedFrom":subQ0}),1.0]])]});}
            var Q62;
            {var subQ0=sQuery(id+"F0.wireOp",EDGE,"E15.41.1");Q62=makeQuery(id+"F0.imprint","IMPRINT",FACE,{"disambiguationData":[TD([[makeQuery(id+"F0.imprint","IMPRINT",EDGE,{"derivedFrom":subQ0}),1.0]])]});}
            var Q63;
            {var subQ0=sQuery(id+"F0.wireOp",EDGE,"E15.16.1");Q63=makeQuery(id+"F0.imprint","IMPRINT",FACE,{"disambiguationData":[TD([[makeQuery(id+"F0.imprint","IMPRINT",EDGE,{"derivedFrom":subQ0}),1.0]])]});}
            var Q64;
            {var subQ0=sQuery(id+"F0.wireOp",EDGE,"E15.42.1");Q64=makeQuery(id+"F0.imprint","IMPRINT",FACE,{"disambiguationData":[TD([[makeQuery(id+"F0.imprint","IMPRINT",EDGE,{"derivedFrom":subQ0}),1.0]])]});}
            var Q65;
            {var subQ0=sQuery(id+"F0.wireOp",EDGE,"E15.29.1");Q65=makeQuery(id+"F0.imprint","IMPRINT",FACE,{"disambiguationData":[TD([[makeQuery(id+"F0.imprint","IMPRINT",EDGE,{"derivedFrom":subQ0}),1.0]])]});}
            var Q66;
            {var subQ0=sQuery(id+"F0.wireOp",EDGE,"E15.21.1");Q66=makeQuery(id+"F0.imprint","IMPRINT",FACE,{"disambiguationData":[TD([[makeQuery(id+"F0.imprint","IMPRINT",EDGE,{"derivedFrom":subQ0}),1.0]])]});}
            var Q67;
            {var subQ0=sQuery(id+"F0.wireOp",EDGE,"E15.35.1");Q67=makeQuery(id+"F0.imprint","IMPRINT",FACE,{"disambiguationData":[TD([[makeQuery(id+"F0.imprint","IMPRINT",EDGE,{"derivedFrom":subQ0}),1.0]])]});}
            var Q68;
            {var subQ0=sQuery(id+"F0.wireOp",EDGE,"E15.36.1");Q68=makeQuery(id+"F0.imprint","IMPRINT",FACE,{"disambiguationData":[TD([[makeQuery(id+"F0.imprint","IMPRINT",EDGE,{"derivedFrom":subQ0}),1.0]])]});}
            var Q69;
            {var subQ0=sQuery(id+"F0.wireOp",EDGE,"E15.37.1");Q69=makeQuery(id+"F0.imprint","IMPRINT",FACE,{"disambiguationData":[TD([[makeQuery(id+"F0.imprint","IMPRINT",EDGE,{"derivedFrom":subQ0}),1.0]])]});}
            var Q70;
            {var subQ0=sQuery(id+"F0.wireOp",EDGE,"E15.39.1");Q70=makeQuery(id+"F0.imprint","IMPRINT",FACE,{"disambiguationData":[TD([[makeQuery(id+"F0.imprint","IMPRINT",EDGE,{"derivedFrom":subQ0}),1.0]])]});}
            var Q71;
            {var subQ0=sQuery(id+"F0.wireOp",EDGE,"E15.38.1");Q71=makeQuery(id+"F0.imprint","IMPRINT",FACE,{"disambiguationData":[TD([[makeQuery(id+"F0.imprint","IMPRINT",EDGE,{"derivedFrom":subQ0}),1.0]])]});}
            var Q72;
            {var subQ0=sQuery(id+"F0.wireOp",EDGE,"E15.33.1");Q72=makeQuery(id+"F0.imprint","IMPRINT",FACE,{"disambiguationData":[TD([[makeQuery(id+"F0.imprint","IMPRINT",EDGE,{"derivedFrom":subQ0}),1.0]])]});}
            var Q73;
            {var subQ0=sQuery(id+"F0.wireOp",EDGE,"E15.34.1");Q73=makeQuery(id+"F0.imprint","IMPRINT",FACE,{"disambiguationData":[TD([[makeQuery(id+"F0.imprint","IMPRINT",EDGE,{"derivedFrom":subQ0}),1.0]])]});}
            var Q74;
            {var subQ0=sQuery(id+"F0.wireOp",EDGE,"E15.3.1");Q74=makeQuery(id+"F0.imprint","IMPRINT",FACE,{"disambiguationData":[TD([[makeQuery(id+"F0.imprint","IMPRINT",EDGE,{"derivedFrom":subQ0}),1.0]])]});}
            var Q75;
            {var subQ0=sQuery(id+"F0.wireOp",EDGE,"E15.19.1");Q75=makeQuery(id+"F0.imprint","IMPRINT",FACE,{"disambiguationData":[TD([[makeQuery(id+"F0.imprint","IMPRINT",EDGE,{"derivedFrom":subQ0}),1.0]])]});}
            var Q76;
            {var subQ0=sQuery(id+"F0.wireOp",EDGE,"E15.27.1");Q76=makeQuery(id+"F0.imprint","IMPRINT",FACE,{"disambiguationData":[TD([[makeQuery(id+"F0.imprint","IMPRINT",EDGE,{"derivedFrom":subQ0}),1.0]])]});}
            var Q77;
            {var subQ0=sQuery(id+"F0.wireOp",EDGE,"E15.25.1");Q77=makeQuery(id+"F0.imprint","IMPRINT",FACE,{"disambiguationData":[TD([[makeQuery(id+"F0.imprint","IMPRINT",EDGE,{"derivedFrom":subQ0}),1.0]])]});}
            var Q78;
            {var subQ0=sQuery(id+"F0.wireOp",EDGE,"E15.26.1");Q78=makeQuery(id+"F0.imprint","IMPRINT",FACE,{"disambiguationData":[TD([[makeQuery(id+"F0.imprint","IMPRINT",EDGE,{"derivedFrom":subQ0}),1.0]])]});}
            var Q79;
            {var subQ0=sQuery(id+"F0.wireOp",EDGE,"E15.18.1");Q79=makeQuery(id+"F0.imprint","IMPRINT",FACE,{"disambiguationData":[TD([[makeQuery(id+"F0.imprint","IMPRINT",EDGE,{"derivedFrom":subQ0}),1.0]])]});}
            var Q80;
            {var subQ1=sQuery(id+"F0.wireOp",EDGE,"E8");Q80=makeQuery(id+"F0.imprint","IMPRINT",FACE,{"disambiguationData":[TD([[makeQuery(id+"F0.imprint","IMPRINT",EDGE,{"derivedFrom":subQ1}),-1.0]])]});}
            var Q81;
            {var subQ0=sQuery(id+"F0.wireOp",EDGE,"E15.1.1");Q81=makeQuery(id+"F0.imprint","IMPRINT",FACE,{"disambiguationData":[TD([[makeQuery(id+"F0.imprint","IMPRINT",EDGE,{"derivedFrom":subQ0}),1.0]])]});}
            var Q82;
            {var subQ0=sQuery(id+"F0.wireOp",EDGE,"E15.9.1");Q82=makeQuery(id+"F0.imprint","IMPRINT",FACE,{"disambiguationData":[TD([[makeQuery(id+"F0.imprint","IMPRINT",EDGE,{"derivedFrom":subQ0}),1.0]])]});}
            var Q83;
            {var subQ0=sQuery(id+"F0.wireOp",EDGE,"E15.17.1");Q83=makeQuery(id+"F0.imprint","IMPRINT",FACE,{"disambiguationData":[TD([[makeQuery(id+"F0.imprint","IMPRINT",EDGE,{"derivedFrom":subQ0}),1.0]])]});}
            var Q84;
            {var subQ0=sQuery(id+"F0.wireOp",EDGE,"E15.4.1");Q84=makeQuery(id+"F0.imprint","IMPRINT",FACE,{"disambiguationData":[TD([[makeQuery(id+"F0.imprint","IMPRINT",EDGE,{"derivedFrom":subQ0}),1.0]])]});}
            var Q85;
            {var subQ0=sQuery(id+"F0.wireOp",EDGE,"E8");Q85=makeQuery(id+"F0.imprint","IMPRINT",FACE,{"disambiguationData":[TD([[makeQuery(id+"F0.imprint","IMPRINT",EDGE,{"derivedFrom":subQ0}),1.0]])]});}
            var Q86;
            {var subQ0=sQuery(id+"F0.wireOp",EDGE,"E15.6.1");Q86=makeQuery(id+"F0.imprint","IMPRINT",FACE,{"disambiguationData":[TD([[makeQuery(id+"F0.imprint","IMPRINT",EDGE,{"derivedFrom":subQ0}),1.0]])]});}
            var Q87;
            Q87=makeQuery(id+"F0.imprint","IMPRINT",FACE,{"disambiguationData":[TD([[makeQuery(id+"F0.imprint","IMPRINT",EDGE,{"derivedFrom":sQuery(id+"F0.wireOp",EDGE,"E3")}),-1.0]])]});
            extrude(context, id + "F1", {"entities" : qUnion([Q0, Q1, Q2, Q3, Q4, Q5, Q6, Q7, Q8, Q9, Q10, Q11, Q12, Q13, Q14, Q15, Q16, Q17, Q18, Q19, Q20, Q21, Q22, Q23, Q24, Q25, Q26, Q27, Q28, Q29, Q30, Q31, Q32, Q33, Q34, Q35, Q36, Q37, Q38, Q39, Q40, Q41, Q42, Q43, Q44, Q45, Q46, Q47, Q48, Q49, Q50, Q51, Q52, Q53, Q54, Q55, Q56, Q57, Q58, Q59, Q60, Q61, Q62, Q63, Q64, Q65, Q66, Q67, Q68, Q69, Q70, Q71, Q72, Q73, Q74, Q75, Q76, Q77, Q78, Q79, Q80, Q81, Q82, Q83, Q84, Q85, Q86, Q87]), "depth" : 9.71 * mm});
        }
        {
            var Q0;
            Q0=makeQuery(id+"F0.imprint","IMPRINT",FACE,{"disambiguationData":[TD([[makeQuery(id+"F0.imprint","IMPRINT",EDGE,{"derivedFrom":sQuery(id+"F0.wireOp",EDGE,"E1")}),-1.0]])]});
            extrude(context, id + "F2", {"entities" : qUnion([Q0]), "depth" : 8 * mm});
        }
        {
            var Q0;
            Q0=makeQuery(id+"F0.imprint","IMPRINT",FACE,{"disambiguationData":[TD([[makeQuery(id+"F0.imprint","IMPRINT",EDGE,{"derivedFrom":sQuery(id+"F0.wireOp",EDGE,"E2")}),1.0]])]});
            var Q1;
            Q1=makeQuery(id+"F0.imprint","IMPRINT",FACE,{"disambiguationData":[TD([[makeQuery(id+"F0.imprint","IMPRINT",EDGE,{"derivedFrom":sQuery(id+"F0.wireOp",EDGE,"E3")}),-1.0]])]});
            extrude(context, id + "F3", {"entities" : qUnion([Q0, Q1]), "operationType" : NewBodyOperationType.ADD, "oppositeDirection" : true, "depth" : 5 * mm});
        }
        {
            var Q0;
            Q0=makeQuery(id+"F3.opExtrude","CAP_FACE",FACE,{"disambiguationData":[OSD([sQuery(id+"F0.wireOp",EDGE,"E3"),sQuery(id+"F0.wireOp",EDGE,"E5"),sQuery(id+"F0.wireOp",EDGE,"E14"),sQuery(id+"F0.wireOp",EDGE,"E15.1.1"),sQuery(id+"F0.wireOp",EDGE,"E15.2.1"),sQuery(id+"F0.wireOp",EDGE,"E15.3.1"),sQuery(id+"F0.wireOp",EDGE,"E15.4.1"),sQuery(id+"F0.wireOp",EDGE,"E15.5.1"),sQuery(id+"F0.wireOp",EDGE,"E15.6.1"),sQuery(id+"F0.wireOp",EDGE,"E15.7.1"),sQuery(id+"F0.wireOp",EDGE,"E15.8.1"),sQuery(id+"F0.wireOp",EDGE,"E15.9.1"),sQuery(id+"F0.wireOp",EDGE,"E15.10.1"),sQuery(id+"F0.wireOp",EDGE,"E15.11.1"),sQuery(id+"F0.wireOp",EDGE,"E15.12.1"),sQuery(id+"F0.wireOp",EDGE,"E15.13.1"),sQuery(id+"F0.wireOp",EDGE,"E15.14.1"),sQuery(id+"F0.wireOp",EDGE,"E15.15.1"),sQuery(id+"F0.wireOp",EDGE,"E15.16.1"),sQuery(id+"F0.wireOp",EDGE,"E15.17.1"),sQuery(id+"F0.wireOp",EDGE,"E15.18.1"),sQuery(id+"F0.wireOp",EDGE,"E15.19.1"),sQuery(id+"F0.wireOp",EDGE,"E15.20.1"),sQuery(id+"F0.wireOp",EDGE,"E15.21.1"),sQuery(id+"F0.wireOp",EDGE,"E15.22.1"),sQuery(id+"F0.wireOp",EDGE,"E15.23.1"),sQuery(id+"F0.wireOp",EDGE,"E15.24.1"),sQuery(id+"F0.wireOp",EDGE,"E15.25.1"),sQuery(id+"F0.wireOp",EDGE,"E15.26.1"),sQuery(id+"F0.wireOp",EDGE,"E15.27.1"),sQuery(id+"F0.wireOp",EDGE,"E15.28.1"),sQuery(id+"F0.wireOp",EDGE,"E15.29.1"),sQuery(id+"F0.wireOp",EDGE,"E15.30.1"),sQuery(id+"F0.wireOp",EDGE,"E15.31.1"),sQuery(id+"F0.wireOp",EDGE,"E15.32.1"),sQuery(id+"F0.wireOp",EDGE,"E15.33.1"),sQuery(id+"F0.wireOp",EDGE,"E15.34.1"),sQuery(id+"F0.wireOp",EDGE,"E15.35.1"),sQuery(id+"F0.wireOp",EDGE,"E15.36.1"),sQuery(id+"F0.wireOp",EDGE,"E15.37.1"),sQuery(id+"F0.wireOp",EDGE,"E15.38.1"),sQuery(id+"F0.wireOp",EDGE,"E15.39.1"),sQuery(id+"F0.wireOp",EDGE,"E15.40.1"),sQuery(id+"F0.wireOp",EDGE,"E15.41.1"),sQuery(id+"F0.wireOp",EDGE,"E15.42.1")])],"isStart":false});
            var sketch = newSketch(context, id + "F4", { "sketchPlane" : qUnion([Q0])});
            skCircle(sketch, "E18", {"center": v(0, 0) * mm, "radius": 17.8 * mm});
            skSolve(sketch);
        }
        {
            var Q0;
            Q0=makeQuery(id+"F4.imprint","IMPRINT",FACE,{"disambiguationData":[TD([[makeQuery(id+"F4.imprint","IMPRINT",EDGE,{"derivedFrom":sQuery(id+"F4.wireOp",EDGE,"E18")}),1.0]])]});
            var Q1;
            Q1=makeQuery(id+"F1.opExtrude","SWEPT_BODY",BODY,{"disambiguationData":[OSD([sQuery(id+"F0.wireOp",EDGE,"E3"),sQuery(id+"F0.wireOp",EDGE,"E5"),sQuery(id+"F0.wireOp",EDGE,"E7"),sQuery(id+"F0.wireOp",EDGE,"E9"),sQuery(id+"F0.wireOp",EDGE,"E10"),sQuery(id+"F0.wireOp",EDGE,"E15.1.0"),sQuery(id+"F0.wireOp",EDGE,"E15.1.2"),sQuery(id+"F0.wireOp",EDGE,"E15.1.3"),sQuery(id+"F0.wireOp",EDGE,"E15.2.0"),sQuery(id+"F0.wireOp",EDGE,"E15.2.2"),sQuery(id+"F0.wireOp",EDGE,"E15.2.3"),sQuery(id+"F0.wireOp",EDGE,"E15.3.0"),sQuery(id+"F0.wireOp",EDGE,"E15.3.2"),sQuery(id+"F0.wireOp",EDGE,"E15.3.3"),sQuery(id+"F0.wireOp",EDGE,"E15.4.0"),sQuery(id+"F0.wireOp",EDGE,"E15.4.2"),sQuery(id+"F0.wireOp",EDGE,"E15.4.3"),sQuery(id+"F0.wireOp",EDGE,"E15.5.0"),sQuery(id+"F0.wireOp",EDGE,"E15.5.2"),sQuery(id+"F0.wireOp",EDGE,"E15.5.3"),sQuery(id+"F0.wireOp",EDGE,"E15.6.0"),sQuery(id+"F0.wireOp",EDGE,"E15.6.2"),sQuery(id+"F0.wireOp",EDGE,"E15.6.3"),sQuery(id+"F0.wireOp",EDGE,"E15.7.0"),sQuery(id+"F0.wireOp",EDGE,"E15.7.2"),sQuery(id+"F0.wireOp",EDGE,"E15.7.3"),sQuery(id+"F0.wireOp",EDGE,"E15.8.0"),sQuery(id+"F0.wireOp",EDGE,"E15.8.2"),sQuery(id+"F0.wireOp",EDGE,"E15.8.3"),sQuery(id+"F0.wireOp",EDGE,"E15.9.0"),sQuery(id+"F0.wireOp",EDGE,"E15.9.2"),sQuery(id+"F0.wireOp",EDGE,"E15.9.3"),sQuery(id+"F0.wireOp",EDGE,"E15.10.0"),sQuery(id+"F0.wireOp",EDGE,"E15.10.2"),sQuery(id+"F0.wireOp",EDGE,"E15.10.3"),sQuery(id+"F0.wireOp",EDGE,"E15.11.0"),sQuery(id+"F0.wireOp",EDGE,"E15.11.2"),sQuery(id+"F0.wireOp",EDGE,"E15.11.3"),sQuery(id+"F0.wireOp",EDGE,"E15.12.0"),sQuery(id+"F0.wireOp",EDGE,"E15.12.2"),sQuery(id+"F0.wireOp",EDGE,"E15.12.3"),sQuery(id+"F0.wireOp",EDGE,"E15.13.0"),sQuery(id+"F0.wireOp",EDGE,"E15.13.2"),sQuery(id+"F0.wireOp",EDGE,"E15.13.3"),sQuery(id+"F0.wireOp",EDGE,"E15.14.0"),sQuery(id+"F0.wireOp",EDGE,"E15.14.2"),sQuery(id+"F0.wireOp",EDGE,"E15.14.3"),sQuery(id+"F0.wireOp",EDGE,"E15.15.0"),sQuery(id+"F0.wireOp",EDGE,"E15.15.2"),sQuery(id+"F0.wireOp",EDGE,"E15.15.3"),sQuery(id+"F0.wireOp",EDGE,"E15.16.0"),sQuery(id+"F0.wireOp",EDGE,"E15.16.2"),sQuery(id+"F0.wireOp",EDGE,"E15.16.3"),sQuery(id+"F0.wireOp",EDGE,"E15.17.0"),sQuery(id+"F0.wireOp",EDGE,"E15.17.2"),sQuery(id+"F0.wireOp",EDGE,"E15.17.3"),sQuery(id+"F0.wireOp",EDGE,"E15.18.0"),sQuery(id+"F0.wireOp",EDGE,"E15.18.2"),sQuery(id+"F0.wireOp",EDGE,"E15.18.3"),sQuery(id+"F0.wireOp",EDGE,"E15.19.0"),sQuery(id+"F0.wireOp",EDGE,"E15.19.2"),sQuery(id+"F0.wireOp",EDGE,"E15.19.3"),sQuery(id+"F0.wireOp",EDGE,"E15.20.0"),sQuery(id+"F0.wireOp",EDGE,"E15.20.2"),sQuery(id+"F0.wireOp",EDGE,"E15.20.3"),sQuery(id+"F0.wireOp",EDGE,"E15.21.0"),sQuery(id+"F0.wireOp",EDGE,"E15.21.2"),sQuery(id+"F0.wireOp",EDGE,"E15.21.3"),sQuery(id+"F0.wireOp",EDGE,"E15.22.0"),sQuery(id+"F0.wireOp",EDGE,"E15.22.2"),sQuery(id+"F0.wireOp",EDGE,"E15.22.3"),sQuery(id+"F0.wireOp",EDGE,"E15.23.0"),sQuery(id+"F0.wireOp",EDGE,"E15.23.2"),sQuery(id+"F0.wireOp",EDGE,"E15.23.3"),sQuery(id+"F0.wireOp",EDGE,"E15.24.0"),sQuery(id+"F0.wireOp",EDGE,"E15.24.2"),sQuery(id+"F0.wireOp",EDGE,"E15.24.3"),sQuery(id+"F0.wireOp",EDGE,"E15.25.0"),sQuery(id+"F0.wireOp",EDGE,"E15.25.2"),sQuery(id+"F0.wireOp",EDGE,"E15.25.3"),sQuery(id+"F0.wireOp",EDGE,"E15.26.0"),sQuery(id+"F0.wireOp",EDGE,"E15.26.2"),sQuery(id+"F0.wireOp",EDGE,"E15.26.3"),sQuery(id+"F0.wireOp",EDGE,"E15.27.0"),sQuery(id+"F0.wireOp",EDGE,"E15.27.2"),sQuery(id+"F0.wireOp",EDGE,"E15.27.3"),sQuery(id+"F0.wireOp",EDGE,"E15.28.0"),sQuery(id+"F0.wireOp",EDGE,"E15.28.2"),sQuery(id+"F0.wireOp",EDGE,"E15.28.3"),sQuery(id+"F0.wireOp",EDGE,"E15.29.0"),sQuery(id+"F0.wireOp",EDGE,"E15.29.2"),sQuery(id+"F0.wireOp",EDGE,"E15.29.3"),sQuery(id+"F0.wireOp",EDGE,"E15.30.0"),sQuery(id+"F0.wireOp",EDGE,"E15.30.2"),sQuery(id+"F0.wireOp",EDGE,"E15.30.3"),sQuery(id+"F0.wireOp",EDGE,"E15.31.0"),sQuery(id+"F0.wireOp",EDGE,"E15.31.2"),sQuery(id+"F0.wireOp",EDGE,"E15.31.3"),sQuery(id+"F0.wireOp",EDGE,"E15.32.0"),sQuery(id+"F0.wireOp",EDGE,"E15.32.2"),sQuery(id+"F0.wireOp",EDGE,"E15.32.3"),sQuery(id+"F0.wireOp",EDGE,"E15.33.0"),sQuery(id+"F0.wireOp",EDGE,"E15.33.2"),sQuery(id+"F0.wireOp",EDGE,"E15.33.3"),sQuery(id+"F0.wireOp",EDGE,"E15.34.0"),sQuery(id+"F0.wireOp",EDGE,"E15.34.2"),sQuery(id+"F0.wireOp",EDGE,"E15.34.3"),sQuery(id+"F0.wireOp",EDGE,"E15.35.0"),sQuery(id+"F0.wireOp",EDGE,"E15.35.2"),sQuery(id+"F0.wireOp",EDGE,"E15.35.3"),sQuery(id+"F0.wireOp",EDGE,"E15.36.0"),sQuery(id+"F0.wireOp",EDGE,"E15.36.2"),sQuery(id+"F0.wireOp",EDGE,"E15.36.3"),sQuery(id+"F0.wireOp",EDGE,"E15.37.0"),sQuery(id+"F0.wireOp",EDGE,"E15.37.2"),sQuery(id+"F0.wireOp",EDGE,"E15.37.3"),sQuery(id+"F0.wireOp",EDGE,"E15.38.0"),sQuery(id+"F0.wireOp",EDGE,"E15.38.2"),sQuery(id+"F0.wireOp",EDGE,"E15.38.3"),sQuery(id+"F0.wireOp",EDGE,"E15.39.0"),sQuery(id+"F0.wireOp",EDGE,"E15.39.2"),sQuery(id+"F0.wireOp",EDGE,"E15.39.3"),sQuery(id+"F0.wireOp",EDGE,"E15.40.0"),sQuery(id+"F0.wireOp",EDGE,"E15.40.2"),sQuery(id+"F0.wireOp",EDGE,"E15.40.3"),sQuery(id+"F0.wireOp",EDGE,"E15.41.0"),sQuery(id+"F0.wireOp",EDGE,"E15.41.2"),sQuery(id+"F0.wireOp",EDGE,"E15.41.3"),sQuery(id+"F0.wireOp",EDGE,"E15.42.0"),sQuery(id+"F0.wireOp",EDGE,"E15.42.2"),sQuery(id+"F0.wireOp",EDGE,"E15.42.3"),sQuery(id+"F0.wireOp",EDGE,"E16"),sQuery(id+"F0.wireOp",EDGE,"E17.1.0"),sQuery(id+"F0.wireOp",EDGE,"E17.2.0"),sQuery(id+"F0.wireOp",EDGE,"E17.3.0"),sQuery(id+"F0.wireOp",EDGE,"E17.4.0"),sQuery(id+"F0.wireOp",EDGE,"E17.5.0"),sQuery(id+"F0.wireOp",EDGE,"E17.6.0"),sQuery(id+"F0.wireOp",EDGE,"E17.7.0"),sQuery(id+"F0.wireOp",EDGE,"E17.8.0"),sQuery(id+"F0.wireOp",EDGE,"E17.9.0"),sQuery(id+"F0.wireOp",EDGE,"E17.10.0"),sQuery(id+"F0.wireOp",EDGE,"E17.11.0"),sQuery(id+"F0.wireOp",EDGE,"E17.12.0"),sQuery(id+"F0.wireOp",EDGE,"E17.13.0"),sQuery(id+"F0.wireOp",EDGE,"E17.14.0"),sQuery(id+"F0.wireOp",EDGE,"E17.15.0"),sQuery(id+"F0.wireOp",EDGE,"E17.16.0"),sQuery(id+"F0.wireOp",EDGE,"E17.17.0"),sQuery(id+"F0.wireOp",EDGE,"E17.18.0"),sQuery(id+"F0.wireOp",EDGE,"E17.19.0"),sQuery(id+"F0.wireOp",EDGE,"E17.20.0"),sQuery(id+"F0.wireOp",EDGE,"E17.21.0"),sQuery(id+"F0.wireOp",EDGE,"E17.22.0"),sQuery(id+"F0.wireOp",EDGE,"E17.23.0"),sQuery(id+"F0.wireOp",EDGE,"E17.24.0"),sQuery(id+"F0.wireOp",EDGE,"E17.25.0"),sQuery(id+"F0.wireOp",EDGE,"E17.26.0"),sQuery(id+"F0.wireOp",EDGE,"E17.27.0"),sQuery(id+"F0.wireOp",EDGE,"E17.28.0"),sQuery(id+"F0.wireOp",EDGE,"E17.29.0"),sQuery(id+"F0.wireOp",EDGE,"E17.30.0"),sQuery(id+"F0.wireOp",EDGE,"E17.31.0"),sQuery(id+"F0.wireOp",EDGE,"E17.32.0"),sQuery(id+"F0.wireOp",EDGE,"E17.33.0"),sQuery(id+"F0.wireOp",EDGE,"E17.34.0"),sQuery(id+"F0.wireOp",EDGE,"E17.35.0"),sQuery(id+"F0.wireOp",EDGE,"E17.36.0"),sQuery(id+"F0.wireOp",EDGE,"E17.37.0"),sQuery(id+"F0.wireOp",EDGE,"E17.38.0"),sQuery(id+"F0.wireOp",EDGE,"E17.39.0"),sQuery(id+"F0.wireOp",EDGE,"E17.40.0"),sQuery(id+"F0.wireOp",EDGE,"E17.41.0"),sQuery(id+"F0.wireOp",EDGE,"E17.42.0")])]});
            extrude(context, id + "F5", {"entities" : qUnion([Q0]), "operationType" : NewBodyOperationType.REMOVE, "endBound" : BoundingType.UP_TO_BODY, "oppositeDirection" : true, "endBoundEntityBody" : qUnion([Q1]), "depth" : 25 * mm});
        }
    });
